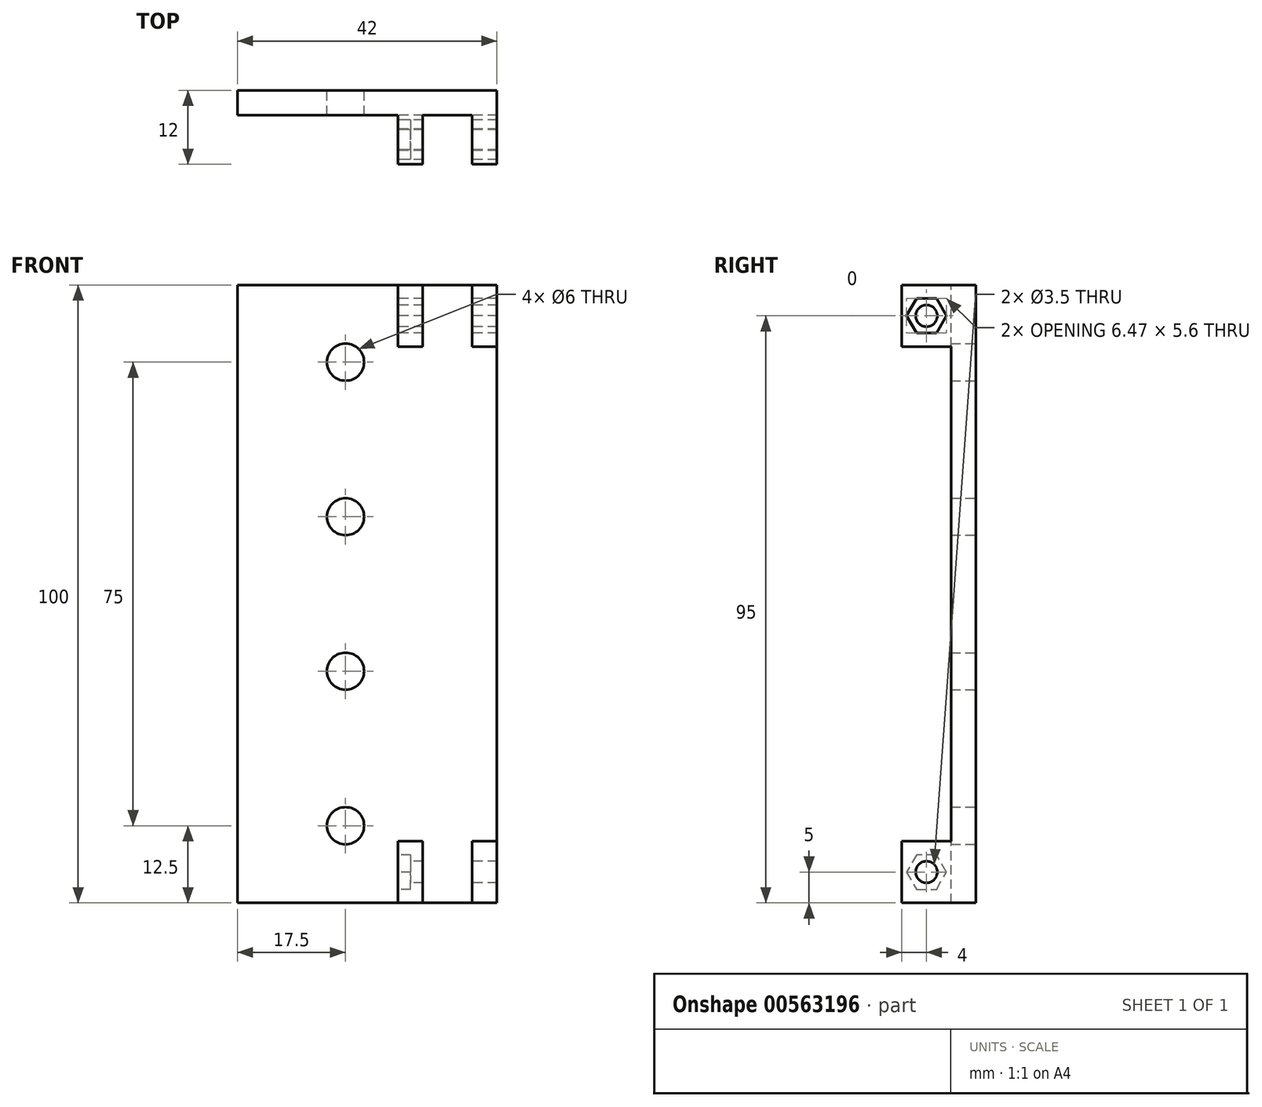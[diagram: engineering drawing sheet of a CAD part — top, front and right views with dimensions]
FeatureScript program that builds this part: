
annotation { "Feature Type Name" : "Feature", "Feature Type Description" : "" }
export const myFeature = defineFeature(function(context is Context, id is Id, definition is map)
    precondition{}
    {
        {
            var Q0;
            Q0=qCreatedBy(makeId("Front.planeOp"),FACE);
            var sketch = newSketch(context, id + "F0", { "sketchPlane" : qUnion([Q0])});
            skLineSegment(sketch, "E0.bottom", {"start": v(0, 0) * mm, "end": v(25, 0) * mm});
            skLineSegment(sketch, "E0.top", {"start": v(0, 100) * mm, "end": v(25, 100) * mm});
            skLineSegment(sketch, "E0.left", {"start": v(0, 0) * mm, "end": v(0, 100) * mm});
            skLineSegment(sketch, "E0.right", {"start": v(25, 0) * mm, "end": v(25, 100) * mm});
            skSolve(sketch);
        }
        {
            var Q0;
            Q0 = qSketchRegion(id + "F0", true);
            extrude(context, id + "F1", {"entities" : qUnion([Q0]), "depth" : 4 * mm, "offsetDistance" : 25 * mm});
        }
        {
            var Q0;
            Q0=makeQuery(id+"F1.opExtrude","CAP_FACE",FACE,{"disambiguationData":[OSD([sQuery(id+"F0.wireOp",EDGE,"E0.bottom"),sQuery(id+"F0.wireOp",EDGE,"E0.top"),sQuery(id+"F0.wireOp",EDGE,"E0.left"),sQuery(id+"F0.wireOp",EDGE,"E0.right")])],"isStart":false});
            var sketch = newSketch(context, id + "F2", { "sketchPlane" : qUnion([Q0])});
            skLineSegment(sketch, "E1.bottom", {"start": v(25, 100) * mm, "end": v(21, 100) * mm});
            skLineSegment(sketch, "E1.top", {"start": v(25, 90) * mm, "end": v(21, 90) * mm});
            skLineSegment(sketch, "E1.left", {"start": v(25, 100) * mm, "end": v(25, 90) * mm});
            skLineSegment(sketch, "E1.right", {"start": v(21, 100) * mm, "end": v(21, 90) * mm});
            skLineSegment(sketch, "E2", {"start": v(25, 50) * mm, "end": v(0, 50) * mm, "construction": true});
            skLineSegment(sketch, "E3.MirrorCS", {"start": v(21, 0) * mm, "end": v(21, 10) * mm});
            skLineSegment(sketch, "E4.MirrorCS", {"start": v(25, 0) * mm, "end": v(25, 10) * mm});
            skLineSegment(sketch, "E5.MirrorCS", {"start": v(25, 10) * mm, "end": v(21, 10) * mm});
            skLineSegment(sketch, "E6.MirrorCS", {"start": v(25, 0) * mm, "end": v(21, 0) * mm});
            skSolve(sketch);
        }
        {
            var Q0;
            Q0=makeQuery(id+"F2.imprint","IMPRINT",FACE,{"disambiguationData":[TD([[makeQuery(id+"F2.imprint","IMPRINT",EDGE,{"derivedFrom":sQuery(id+"F2.wireOp",EDGE,"E1.bottom")}),-1.0]])]});
            var Q1;
            Q1=makeQuery(id+"F2.imprint","IMPRINT",FACE,{"disambiguationData":[TD([[makeQuery(id+"F2.imprint","IMPRINT",EDGE,{"derivedFrom":sQuery(id+"F2.wireOp",EDGE,"E3.MirrorCS")}),-1.0]])]});
            extrude(context, id + "F3", {"entities" : qUnion([Q0, Q1]), "operationType" : NewBodyOperationType.ADD, "depth" : 8 * mm, "offsetDistance" : 25 * mm});
        }
        {
            var Q0;
            Q0=makeQuery(id+"F1.opExtrude","CAP_FACE",FACE,{"disambiguationData":[OSD([sQuery(id+"F0.wireOp",EDGE,"E0.bottom"),sQuery(id+"F0.wireOp",EDGE,"E0.top"),sQuery(id+"F0.wireOp",EDGE,"E0.left"),sQuery(id+"F0.wireOp",EDGE,"E0.right")])],"isStart":true});
            var sketch = newSketch(context, id + "F4", { "sketchPlane" : qUnion([Q0])});
            skCircle(sketch, "E7", {"center": v(-12.5, 87.5) * mm, "radius": 3 * mm});
            skPoint(sketch, "E7.centerSnap0", {"position": v(-12.5, 100) * mm});
            skCircle(sketch, "E8", {"center": v(-12.5, 62.5) * mm, "radius": 3 * mm});
            skCircle(sketch, "E9", {"center": v(-12.5, 37.5) * mm, "radius": 3 * mm});
            skCircle(sketch, "E10", {"center": v(-12.5, 12.5) * mm, "radius": 3 * mm});
            skLineSegment(sketch, "E11", {"start": v(-25, 50) * mm, "end": v(0, 50) * mm, "construction": true});
            skSolve(sketch);
        }
        {
            var Q0;
            Q0=makeQuery(id+"F1.opExtrude","SWEPT_FACE",FACE,{"disambiguationData":[OSD([sQuery(id+"F0.wireOp",EDGE,"E0.left")])]});
            extrude(context, id + "F5", {"entities" : qUnion([Q0]), "operationType" : NewBodyOperationType.ADD, "depth" : 5 * mm, "offsetDistance" : 25 * mm});
        }
        {
            var Q0;
            Q0=makeQuery(id+"F4.imprint","IMPRINT",FACE,{"disambiguationData":[TD([[makeQuery(id+"F4.imprint","IMPRINT",EDGE,{"derivedFrom":sQuery(id+"F4.wireOp",EDGE,"E10")}),1.0]])]});
            var Q1;
            Q1=makeQuery(id+"F4.imprint","IMPRINT",FACE,{"disambiguationData":[TD([[makeQuery(id+"F4.imprint","IMPRINT",EDGE,{"derivedFrom":sQuery(id+"F4.wireOp",EDGE,"E9")}),1.0]])]});
            var Q2;
            Q2=makeQuery(id+"F4.imprint","IMPRINT",FACE,{"disambiguationData":[TD([[makeQuery(id+"F4.imprint","IMPRINT",EDGE,{"derivedFrom":sQuery(id+"F4.wireOp",EDGE,"E8")}),1.0]])]});
            var Q3;
            Q3=makeQuery(id+"F4.imprint","IMPRINT",FACE,{"disambiguationData":[TD([[makeQuery(id+"F4.imprint","IMPRINT",EDGE,{"derivedFrom":sQuery(id+"F4.wireOp",EDGE,"E7")}),1.0]])]});
            extrude(context, id + "F6", {"entities" : qUnion([Q0, Q1, Q2, Q3]), "operationType" : NewBodyOperationType.REMOVE, "oppositeDirection" : true, "depth" : 25 * mm, "offsetDistance" : 25 * mm});
        }
        {
            var Q0;
            Q0=makeQuery(id+"F3.boolean.opBoolean","MERGE",FACE,{"derivedFrom":[makeQuery(id+"F1.opExtrude","SWEPT_FACE",FACE,{"disambiguationData":[OSD([sQuery(id+"F0.wireOp",EDGE,"E0.right")])]}),makeQuery(id+"F3.opExtrude","SWEPT_FACE",FACE,{"disambiguationData":[OSD([sQuery(id+"F2.wireOp",EDGE,"E1.left")])]}),makeQuery(id+"F3.opExtrude","SWEPT_FACE",FACE,{"disambiguationData":[OSD([sQuery(id+"F2.wireOp",EDGE,"E4.MirrorCS")])]})]});
            var sketch = newSketch(context, id + "F7", { "sketchPlane" : qUnion([Q0])});
            skLineSegment(sketch, "E12.0.0", {"start": v(0, 0) * mm, "end": v(0, 100) * mm});
            skLineSegment(sketch, "E12.0.1", {"start": v(0, 100) * mm, "end": v(-12, 100) * mm});
            skLineSegment(sketch, "E12.0.2", {"start": v(-12, 100) * mm, "end": v(-12, 90) * mm});
            skLineSegment(sketch, "E12.0.3", {"start": v(-12, 90) * mm, "end": v(-4, 90) * mm});
            skLineSegment(sketch, "E12.0.4", {"start": v(-4, 90) * mm, "end": v(-4, 10) * mm});
            skLineSegment(sketch, "E12.0.5", {"start": v(-4, 10) * mm, "end": v(-12, 10) * mm});
            skLineSegment(sketch, "E12.0.6", {"start": v(-12, 10) * mm, "end": v(-12, 0) * mm});
            skLineSegment(sketch, "E12.0.7", {"start": v(-12, 0) * mm, "end": v(0, 0) * mm});
            skLineSegment(sketch, "E13", {"start": v(-4, 0) * mm, "end": v(-4, 100) * mm});
            skSolve(sketch);
        }
        {
            var Q0;
            {var subQ4=sQuery(id+"F7.wireOp",EDGE,"E12.0.0");Q0=makeQuery(id+"F7.imprint","IMPRINT",FACE,{"disambiguationData":[TD([[makeQuery(id+"F7.imprint","IMPRINT",EDGE,{"derivedFrom":subQ4}),1.0]])]});}
            extrude(context, id + "F8", {"entities" : qUnion([Q0]), "operationType" : NewBodyOperationType.ADD, "depth" : 12 * mm, "offsetDistance" : 25 * mm});
        }
        {
            var Q0;
            {var subQ0=sQuery(id+"F0.wireOp",EDGE,"E0.left");Q0=makeQuery(id+"F8.boolean.opBoolean","MERGE",FACE,{"derivedFrom":[makeQuery(id+"F5.boolean.opBoolean","MERGE",FACE,{"derivedFrom":[makeQuery(id+"F1.opExtrude","CAP_FACE",FACE,{"disambiguationData":[OSD([sQuery(id+"F0.wireOp",EDGE,"E0.bottom"),sQuery(id+"F0.wireOp",EDGE,"E0.top"),subQ0,sQuery(id+"F0.wireOp",EDGE,"E0.right")])],"isStart":false}),makeQuery(id+"F5.opExtrude","SWEPT_FACE",FACE,{"disambiguationData":[OSD([subQ0]),TDD([makeQuery(id+"F1.opExtrude","CAP_EDGE",EDGE,{"disambiguationData":[OSD([subQ0])],"isStart":false})])]})]}),makeQuery(id+"F8.opExtrude","SWEPT_FACE",FACE,{"disambiguationData":[OSD([sQuery(id+"F7.wireOp",EDGE,"E13")])]})]});}
            var sketch = newSketch(context, id + "F9", { "sketchPlane" : qUnion([Q0])});
            skLineSegment(sketch, "E14.bottom", {"start": v(37, 0) * mm, "end": v(33, 0) * mm});
            skLineSegment(sketch, "E14.top", {"start": v(37, 100) * mm, "end": v(33, 100) * mm});
            skLineSegment(sketch, "E14.left", {"start": v(37, 0) * mm, "end": v(37, 100) * mm});
            skLineSegment(sketch, "E14.right", {"start": v(33, 0) * mm, "end": v(33, 100) * mm});
            skSolve(sketch);
        }
        {
            var Q0;
            Q0 = qSketchRegion(id + "F9", true);
            var Q1;
            Q1=makeQuery(id+"F3.opExtrude","CAP_FACE",FACE,{"disambiguationData":[OSD([sQuery(id+"F2.wireOp",EDGE,"E1.bottom"),sQuery(id+"F2.wireOp",EDGE,"E1.top"),sQuery(id+"F2.wireOp",EDGE,"E1.left"),sQuery(id+"F2.wireOp",EDGE,"E1.right")])],"isStart":false});
            extrude(context, id + "F10", {"entities" : qUnion([Q0]), "operationType" : NewBodyOperationType.ADD, "endBound" : BoundingType.UP_TO_SURFACE, "depth" : 25 * mm, "endBoundEntityFace" : qUnion([Q1]), "offsetDistance" : 25 * mm});
        }
        {
            var Q0;
            Q0=makeQuery(id+"F10.opExtrude","SWEPT_FACE",FACE,{"disambiguationData":[OSD([sQuery(id+"F9.wireOp",EDGE,"E14.right")])]});
            var sketch = newSketch(context, id + "F11", { "sketchPlane" : qUnion([Q0])});
            skLineSegment(sketch, "E15.0", {"start": v(12, 90) * mm, "end": v(4, 90) * mm});
            skLineSegment(sketch, "E16.0", {"start": v(12, 0) * mm, "end": v(12, 100) * mm});
            skLineSegment(sketch, "E17.0", {"start": v(4, 0) * mm, "end": v(4, 100) * mm});
            skLineSegment(sketch, "E18.0", {"start": v(12, 10) * mm, "end": v(4, 10) * mm});
            skSolve(sketch);
        }
        {
            var Q0;
            Q0 = qSketchRegion(id + "F11", true);
            extrude(context, id + "F12", {"entities" : qUnion([Q0]), "operationType" : NewBodyOperationType.REMOVE, "oppositeDirection" : true, "depth" : 25 * mm, "offsetDistance" : 25 * mm});
        }
        {
            var Q0;
            Q0=makeQuery(id+"F3.opExtrude","SWEPT_FACE",FACE,{"disambiguationData":[OSD([sQuery(id+"F2.wireOp",EDGE,"E3.MirrorCS")])]});
            var sketch = newSketch(context, id + "F13", { "sketchPlane" : qUnion([Q0])});
            skCircle(sketch, "E19.cCircle", {"center": v(8, 5) * mm, "radius": 2.8 * mm, "construction": true});
            skPoint(sketch, "E19.cCircle.centerSnap0", {"position": v(8, 0) * mm});
            skPoint(sketch, "E19.cCircle.centerSnap1", {"position": v(12, 5) * mm});
            skLineSegment(sketch, "E19.0", {"start": v(9.62, 7.8) * mm, "end": v(11.23, 5) * mm});
            skLineSegment(sketch, "E19.1", {"start": v(11.23, 5) * mm, "end": v(9.62, 2.2) * mm});
            skLineSegment(sketch, "E19.2", {"start": v(9.62, 2.2) * mm, "end": v(6.38, 2.2) * mm});
            skLineSegment(sketch, "E19.3", {"start": v(6.38, 2.2) * mm, "end": v(4.77, 5) * mm});
            skLineSegment(sketch, "E19.4", {"start": v(4.77, 5) * mm, "end": v(6.38, 7.8) * mm});
            skLineSegment(sketch, "E19.5", {"start": v(6.38, 7.8) * mm, "end": v(9.62, 7.8) * mm});
            skPoint(sketch, "E19.0.midPoint", {"position": v(10.42, 6.4) * mm});
            skCircle(sketch, "E20", {"center": v(8, 5) * mm, "radius": 1.75 * mm});
            skPoint(sketch, "E21.0", {"position": v(0, 50) * mm});
            skLineSegment(sketch, "E22", {"start": v(0, 50) * mm, "end": v(12.8, 50) * mm, "construction": true});
            skLineSegment(sketch, "E23.MirrorCS", {"start": v(11.23, 95) * mm, "end": v(9.62, 97.8) * mm});
            skLineSegment(sketch, "E24.MirrorCS", {"start": v(9.62, 97.8) * mm, "end": v(6.38, 97.8) * mm});
            skLineSegment(sketch, "E25.MirrorCS", {"start": v(6.38, 92.2) * mm, "end": v(9.62, 92.2) * mm});
            skLineSegment(sketch, "E26.MirrorCS", {"start": v(9.62, 92.2) * mm, "end": v(11.23, 95) * mm});
            skPoint(sketch, "E27.MirrorP", {"position": v(8, 100) * mm});
            skLineSegment(sketch, "E28.MirrorCS", {"start": v(6.38, 97.8) * mm, "end": v(4.77, 95) * mm});
            skLineSegment(sketch, "E29.MirrorCS", {"start": v(4.77, 95) * mm, "end": v(6.38, 92.2) * mm});
            skCircle(sketch, "E30.MirrorC", {"center": v(8, 95) * mm, "radius": 1.75 * mm});
            skPoint(sketch, "E31.MirrorP", {"position": v(10.42, 93.6) * mm});
            skPoint(sketch, "E32.MirrorP", {"position": v(12, 95) * mm});
            skCircle(sketch, "E33.MirrorC", {"center": v(8, 95) * mm, "radius": 2.8 * mm, "construction": true});
            skSolve(sketch);
        }
        {
            var Q0;
            Q0 = qSketchRegion(id + "F13", true);
            extrude(context, id + "F14", {"entities" : qUnion([Q0]), "operationType" : NewBodyOperationType.REMOVE, "oppositeDirection" : true, "depth" : 2 * mm, "offsetDistance" : 25 * mm});
        }
        {
            var Q0;
            Q0=makeQuery(id+"F13.imprint","IMPRINT",FACE,{"disambiguationData":[TD([[makeQuery(id+"F13.imprint","IMPRINT",EDGE,{"derivedFrom":sQuery(id+"F13.wireOp",EDGE,"E20")}),1.0]])]});
            var Q1;
            Q1=makeQuery(id+"F13.imprint","IMPRINT",FACE,{"disambiguationData":[TD([[makeQuery(id+"F13.imprint","IMPRINT",EDGE,{"derivedFrom":sQuery(id+"F13.wireOp",EDGE,"E30.MirrorC")}),-1.0]])]});
            extrude(context, id + "F15", {"entities" : qUnion([Q0, Q1]), "operationType" : NewBodyOperationType.REMOVE, "oppositeDirection" : true, "depth" : 25 * mm, "offsetDistance" : 25 * mm});
        }
    });
